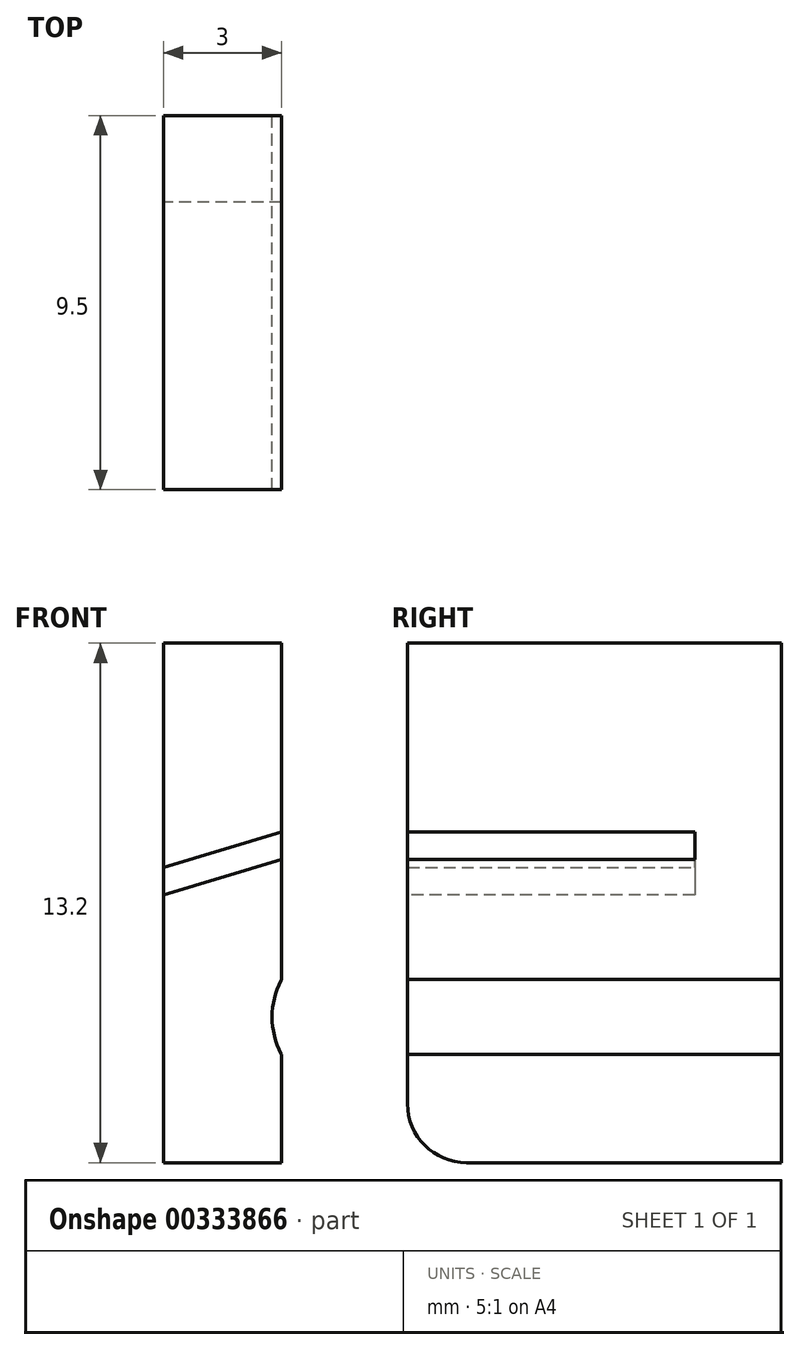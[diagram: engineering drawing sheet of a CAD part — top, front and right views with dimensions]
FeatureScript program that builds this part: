
annotation { "Feature Type Name" : "Feature", "Feature Type Description" : "" }
export const myFeature = defineFeature(function(context is Context, id is Id, definition is map)
    precondition{}
    {
        {
            var Q0;
            Q0=qCreatedBy(makeId("Front.planeOp"),FACE);
            var sketch = newSketch(context, id + "F0", { "sketchPlane" : qUnion([Q0])});
            skLineSegment(sketch, "E0.bottom", {"start": v(0, 0) * mm, "end": v(4, 0) * mm});
            skLineSegment(sketch, "E0.left", {"start": v(0, 0) * mm, "end": v(0, 4) * mm});
            skLineSegment(sketch, "E0.right", {"start": v(4, 0) * mm, "end": v(4, 1.55) * mm});
            skLineSegment(sketch, "E1", {"start": v(0, 2.5) * mm, "end": v(-3.1, 2.5) * mm});
            skPoint(sketch, "E2.visualSharp", {"position": v(4, 2.5) * mm});
            skLineSegment(sketch, "E3", {"start": v(4, 2.5) * mm, "end": v(3.5, 2.5) * mm});
            skLineSegment(sketch, "E4", {"start": v(4, 3.43) * mm, "end": v(4, 3.45) * mm});
            skLineSegment(sketch, "E5.MirrorCS", {"start": v(4, 1.57) * mm, "end": v(4, 1.55) * mm});
            skPoint(sketch, "E6.visualSharp", {"position": v(3.5, 2.5) * mm});
            skArc(sketch, "E6.filletArc", {"start": v(4, 3.43) * mm, "mid": v(3.76, 2.5) * mm, "end": v(4, 1.57) * mm});
            skPoint(sketch, "E7.orphan", {"position": v(5.5, -1.3) * mm});
            skPoint(sketch, "E8.end.orphan", {"position": v(5.5, 6.3) * mm});
            skLineSegment(sketch, "E9", {"start": v(-1, 4) * mm, "end": v(-1, 0) * mm});
            skLineSegment(sketch, "E10", {"start": v(-1, 0) * mm, "end": v(0, 0) * mm});
            skLineSegment(sketch, "E11", {"start": v(4, 1.55) * mm, "end": v(4, -1.5) * mm});
            skLineSegment(sketch, "E12", {"start": v(4, -1.5) * mm, "end": v(-1, 0) * mm});
            skLineSegment(sketch, "E13.top", {"start": v(4, 4) * mm, "end": v(-1, 4) * mm});
            skPoint(sketch, "E14.orphan", {"position": v(4, 5) * mm});
            skPoint(sketch, "E15.orphan", {"position": v(0, 5) * mm});
            skLineSegment(sketch, "E16.trimOffspring", {"start": v(4, 3.45) * mm, "end": v(4, 4) * mm});
            skSolve(sketch);
        }
        {
            var Q0;
            Q0=qSketchRegion(id+"F0",true);
            extrude(context, id + "F1", {"entities" : qUnion([Q0]), "depth" : 10 * mm});
        }
        {
            var Q0;
            Q0=makeQuery(id+"F1.opExtrude","SWEPT_FACE",FACE,{"disambiguationData":[OSD([sQuery(id+"F0.wireOp",EDGE,"E13.top")])]});
            cPlane(context, id + "F2", {"entities" : qUnion([Q0]), "cplaneType" : CPlaneType.OFFSET, "offset" : 3 * mm, "oppositeDirection" : true, "width" : 150 * mm, "height" : 150 * mm});
        }
        {
            var Q0;
            Q0=qCreatedBy(id+"F2.planeOp",FACE);
            var sketch = newSketch(context, id + "F3", { "sketchPlane" : qUnion([Q0])});
            skLineSegment(sketch, "E17.bottom", {"start": v(0, 0) * mm, "end": v(4, 0) * mm});
            skLineSegment(sketch, "E17.top", {"start": v(0, -2.7) * mm, "end": v(4, -2.7) * mm});
            skLineSegment(sketch, "E17.left", {"start": v(0, 0) * mm, "end": v(0, -2.7) * mm});
            skLineSegment(sketch, "E17.right", {"start": v(4, 0) * mm, "end": v(4, -2.7) * mm});
            skLineSegment(sketch, "E18.bottom", {"start": v(0, 0) * mm, "end": v(-1, 0) * mm});
            skLineSegment(sketch, "E18.top", {"start": v(0, -2.7) * mm, "end": v(-1, -2.7) * mm});
            skLineSegment(sketch, "E18.right", {"start": v(-1, 0) * mm, "end": v(-1, -2.7) * mm});
            skSolve(sketch);
        }
        {
            var Q0;
            Q0=qSketchRegion(id+"F3",true);
            extrude(context, id + "F4", {"entities" : qUnion([Q0]), "operationType" : NewBodyOperationType.ADD, "oppositeDirection" : true, "depth" : 7 * mm});
        }
        {
            var Q0;
            Q0=makeQuery(id+"F4.opExtrude","SWEPT_FACE",FACE,{"disambiguationData":[OSD([sQuery(id+"F3.wireOp",EDGE,"E17.top"),sQuery(id+"F3.wireOp",EDGE,"E18.top")])]});
            var sketch = newSketch(context, id + "F5", { "sketchPlane" : qUnion([Q0])});
            skLineSegment(sketch, "E19", {"start": v(4, -6) * mm, "end": v(4, -2.2) * mm});
            skLineSegment(sketch, "E20", {"start": v(-1, -6) * mm, "end": v(-1, -0.7) * mm});
            skLineSegment(sketch, "E21", {"start": v(-1, -0.7) * mm, "end": v(4, -2.2) * mm});
            skLineSegment(sketch, "E22", {"start": v(-1, -6) * mm, "end": v(4, -6) * mm});
            skSolve(sketch);
        }
        {
            var Q0;
            Q0=qSketchRegion(id+"F5",true);
            var Q1;
            Q1=makeQuery(id+"F1.opExtrude","CAP_FACE",FACE,{"disambiguationData":[OSD([sQuery(id+"F0.wireOp",EDGE,"E4"),sQuery(id+"F0.wireOp",EDGE,"E5.MirrorCS"),sQuery(id+"F0.wireOp",EDGE,"E6.filletArc"),sQuery(id+"F0.wireOp",EDGE,"E9"),sQuery(id+"F0.wireOp",EDGE,"E11"),sQuery(id+"F0.wireOp",EDGE,"E12"),sQuery(id+"F0.wireOp",EDGE,"E13.top"),sQuery(id+"F0.wireOp",EDGE,"E16.trimOffspring")])],"isStart":false});
            extrude(context, id + "F6", {"entities" : qUnion([Q0]), "operationType" : NewBodyOperationType.ADD, "endBound" : BoundingType.UP_TO_SURFACE, "endBoundEntityFace" : qUnion([Q1]), "depth" : 25 * mm});
        }
        {
            var Q0;
            Q0=makeQuery(id+"F6.boolean.opBoolean","MERGE",FACE,{"derivedFrom":[makeQuery(id+"F4.opExtrude","CAP_FACE",FACE,{"disambiguationData":[OSD([sQuery(id+"F3.wireOp",EDGE,"E17.bottom"),sQuery(id+"F3.wireOp",EDGE,"E17.top"),sQuery(id+"F3.wireOp",EDGE,"E17.right"),sQuery(id+"F3.wireOp",EDGE,"E18.bottom"),sQuery(id+"F3.wireOp",EDGE,"E18.top"),sQuery(id+"F3.wireOp",EDGE,"E18.right")])],"isStart":false}),makeQuery(id+"F6.opExtrude","SWEPT_FACE",FACE,{"disambiguationData":[OSD([sQuery(id+"F5.wireOp",EDGE,"E22")])]})]});
            extrude(context, id + "F7", {"entities" : qUnion([Q0]), "operationType" : NewBodyOperationType.ADD, "depth" : 1 * mm});
        }
        {
            var Q0;
            Q0=makeQuery(id+"F1.opExtrude","SWEPT_FACE",FACE,{"disambiguationData":[OSD([sQuery(id+"F0.wireOp",EDGE,"E13.top")])]});
            extrude(context, id + "F8", {"entities" : qUnion([Q0]), "operationType" : NewBodyOperationType.ADD, "depth" : 0.5 * mm});
        }
        {
            var Q0;
            {var subQ0=sQuery(id+"F0.wireOp",EDGE,"E13.top");var subQ1=sQuery(id+"F3.wireOp",EDGE,"E18.bottom");var subQ2=sQuery(id+"F3.wireOp",EDGE,"E17.bottom");Q0=makeQuery(id+"F8.boolean.opBoolean","MERGE",FACE,{"derivedFrom":[makeQuery(id+"F7.boolean.opBoolean","MERGE",FACE,{"derivedFrom":[makeQuery(id+"F4.boolean.opBoolean","MERGE",FACE,{"derivedFrom":[makeQuery(id+"F1.opExtrude","CAP_FACE",FACE,{"disambiguationData":[OSD([sQuery(id+"F0.wireOp",EDGE,"E4"),sQuery(id+"F0.wireOp",EDGE,"E5.MirrorCS"),sQuery(id+"F0.wireOp",EDGE,"E6.filletArc"),sQuery(id+"F0.wireOp",EDGE,"E9"),sQuery(id+"F0.wireOp",EDGE,"E11"),sQuery(id+"F0.wireOp",EDGE,"E12"),subQ0,sQuery(id+"F0.wireOp",EDGE,"E16.trimOffspring")])],"isStart":true}),makeQuery(id+"F4.opExtrude","SWEPT_FACE",FACE,{"disambiguationData":[OSD([subQ2,subQ1])]})]}),makeQuery(id+"F7.opExtrude","SWEPT_FACE",FACE,{"disambiguationData":[OSD([subQ2,subQ1])]})]}),makeQuery(id+"F8.opExtrude","SWEPT_FACE",FACE,{"disambiguationData":[OSD([subQ0]),TDD([makeQuery(id+"F1.opExtrude","CAP_EDGE",EDGE,{"disambiguationData":[OSD([subQ0])],"isStart":true})])]})]});}
            extrude(context, id + "F9", {"entities" : qUnion([Q0]), "operationType" : NewBodyOperationType.REMOVE, "oppositeDirection" : true, "depth" : 0.5 * mm});
        }
        {
            var Q0;
            Q0=makeQuery(id+"F8.opExtrude","CAP_FACE",FACE,{"disambiguationData":[OSD([sQuery(id+"F0.wireOp",EDGE,"E13.top")])],"isStart":false});
            extrude(context, id + "F10", {"entities" : qUnion([Q0]), "operationType" : NewBodyOperationType.ADD, "depth" : 0.5 * mm});
        }
        {
            var Q0;
            {var subQ0=sQuery(id+"F5.wireOp",EDGE,"E22");var subQ1=sQuery(id+"F0.wireOp",EDGE,"E16.trimOffspring");var subQ2=sQuery(id+"F0.wireOp",EDGE,"E13.top");var subQ3=sQuery(id+"F0.wireOp",EDGE,"E12");var subQ4=sQuery(id+"F0.wireOp",EDGE,"E11");var subQ5=sQuery(id+"F0.wireOp",EDGE,"E9");var subQ6=sQuery(id+"F0.wireOp",EDGE,"E6.filletArc");var subQ7=sQuery(id+"F0.wireOp",EDGE,"E5.MirrorCS");var subQ8=sQuery(id+"F0.wireOp",EDGE,"E4");Q0=makeQuery(id+"FcvEmVvv3j6Bp3b_1.boolean.opBoolean","MERGE",FACE,{"derivedFrom":[makeQuery(id+"F7.boolean.opBoolean","MERGE",FACE,{"derivedFrom":[makeQuery(id+"F6.opExtrude","CAP_FACE",FACE,{"disambiguationData":[OSD([subQ8,subQ7,subQ6,subQ5,subQ4,subQ3,subQ2,subQ1])],"isStart":false}),makeQuery(id+"F7.opExtrude","SWEPT_FACE",FACE,{"disambiguationData":[OSD([subQ8,subQ7,subQ6,subQ5,subQ4,subQ3,subQ2,subQ1,subQ0])]})]}),makeQuery(id+"FcvEmVvv3j6Bp3b_1.opExtrude","SWEPT_FACE",FACE,{"disambiguationData":[OSD([subQ8,subQ7,subQ6,subQ5,subQ4,subQ3,subQ2,subQ1,subQ0])]})]});}
            var sketch = newSketch(context, id + "F11", { "sketchPlane" : qUnion([Q0])});
            skLineSegment(sketch, "E23.bottom", {"start": v(-1, -8) * mm, "end": v(1, -8) * mm});
            skLineSegment(sketch, "E23.top", {"start": v(-1, 6.98) * mm, "end": v(1, 6.98) * mm});
            skLineSegment(sketch, "E23.left", {"start": v(-1, -8) * mm, "end": v(-1, 6.98) * mm});
            skLineSegment(sketch, "E23.right", {"start": v(1, -8) * mm, "end": v(1, 6.98) * mm});
            skSolve(sketch);
        }
        {
            var Q0;
            Q0=qSketchRegion(id+"F11",true);
            extrude(context, id + "F12", {"entities" : qUnion([Q0]), "operationType" : NewBodyOperationType.REMOVE, "oppositeDirection" : true, "depth" : 25 * mm});
        }
        {
            var Q0;
            Q0=makeQuery(id+"F10.opExtrude","CAP_FACE",FACE,{"disambiguationData":[OSD([sQuery(id+"F0.wireOp",EDGE,"E13.top")])],"isStart":false});
            extrude(context, id + "F13", {"entities" : qUnion([Q0]), "operationType" : NewBodyOperationType.ADD, "depth" : 1.2 * mm});
        }
        {
            var Q0;
            {var subQ0=sQuery(id+"F0.wireOp",EDGE,"E13.top");Q0=makeQuery(id+"F13.opExtrude","CAP_EDGE",EDGE,{"disambiguationData":[OSD([subQ0]),TDD([makeQuery(id+"F10.opExtrude","CAP_EDGE",EDGE,{"disambiguationData":[OSD([subQ0]),TDD([makeQuery(id+"F8.opExtrude","CAP_EDGE",EDGE,{"disambiguationData":[OSD([subQ0]),TDD([makeQuery(id+"F1.opExtrude","CAP_EDGE",EDGE,{"disambiguationData":[OSD([subQ0])],"isStart":false})])],"isStart":false})])],"isStart":false})])],"isStart":false});}
            var Q1;
            {var subQ0=sQuery(id+"F0.wireOp",EDGE,"E13.top");Q1=makeQuery(id+"F13.opExtrude","CAP_EDGE",EDGE,{"disambiguationData":[OSD([subQ0]),TDD([makeQuery(id+"F10.opExtrude","CAP_EDGE",EDGE,{"disambiguationData":[OSD([subQ0]),TDD([makeQuery(id+"F9.boolean.opBoolean","COPY",EDGE,{"derivedFrom":makeQuery(id+"F9.opExtrude","CAP_EDGE",EDGE,{"disambiguationData":[OSD([subQ0])],"isStart":false})})])],"isStart":false})])],"isStart":false});}
            fillet(context, id + "F14", {"entities" : qUnion([Q0, Q1]), "radius" : 1.5 * mm, "tangentPropagation" : true, "allowEdgeOverflow" : false});
        }
        {
            var Q0;
            Q0=makeQuery(id+"F7.opExtrude","CAP_FACE",FACE,{"disambiguationData":[OSD([sQuery(id+"F3.wireOp",EDGE,"E17.bottom"),sQuery(id+"F3.wireOp",EDGE,"E17.top"),sQuery(id+"F3.wireOp",EDGE,"E17.right"),sQuery(id+"F3.wireOp",EDGE,"E18.bottom"),sQuery(id+"F3.wireOp",EDGE,"E18.top"),sQuery(id+"F3.wireOp",EDGE,"E18.right"),sQuery(id+"F5.wireOp",EDGE,"E22")])],"isStart":false});
            cPlane(context, id + "F15", {"entities" : qUnion([Q0]), "cplaneType" : CPlaneType.OFFSET, "offset" : 1 * mm, "width" : 150 * mm, "height" : 150 * mm});
        }
        {
            var Q0;
            Q0=makeQuery(id+"F1.opExtrude","SWEPT_BODY",BODY,{"disambiguationData":[OSD([sQuery(id+"F0.wireOp",EDGE,"E4"),sQuery(id+"F0.wireOp",EDGE,"E5.MirrorCS"),sQuery(id+"F0.wireOp",EDGE,"E6.filletArc"),sQuery(id+"F0.wireOp",EDGE,"E9"),sQuery(id+"F0.wireOp",EDGE,"E11"),sQuery(id+"F0.wireOp",EDGE,"E12"),sQuery(id+"F0.wireOp",EDGE,"E13.top"),sQuery(id+"F0.wireOp",EDGE,"E16.trimOffspring")])]});
            var Q1;
            Q1=qCreatedBy(id+"F15.planeOp",FACE);
            mirror(context, id + "F16", {"entities" : qUnion([Q0]), "mirrorPlane" : qUnion([Q1])});
        }
        {
            var Q0;
            Q0=makeQuery(id+"F1.opExtrude","SWEPT_BODY",BODY,{"disambiguationData":[OSD([sQuery(id+"F0.wireOp",EDGE,"E4"),sQuery(id+"F0.wireOp",EDGE,"E5.MirrorCS"),sQuery(id+"F0.wireOp",EDGE,"E6.filletArc"),sQuery(id+"F0.wireOp",EDGE,"E9"),sQuery(id+"F0.wireOp",EDGE,"E11"),sQuery(id+"F0.wireOp",EDGE,"E12"),sQuery(id+"F0.wireOp",EDGE,"E13.top"),sQuery(id+"F0.wireOp",EDGE,"E16.trimOffspring")])]});
            deleteBodies(context, id + "F17", {"entities" : qUnion([Q0])});
        }
    });
